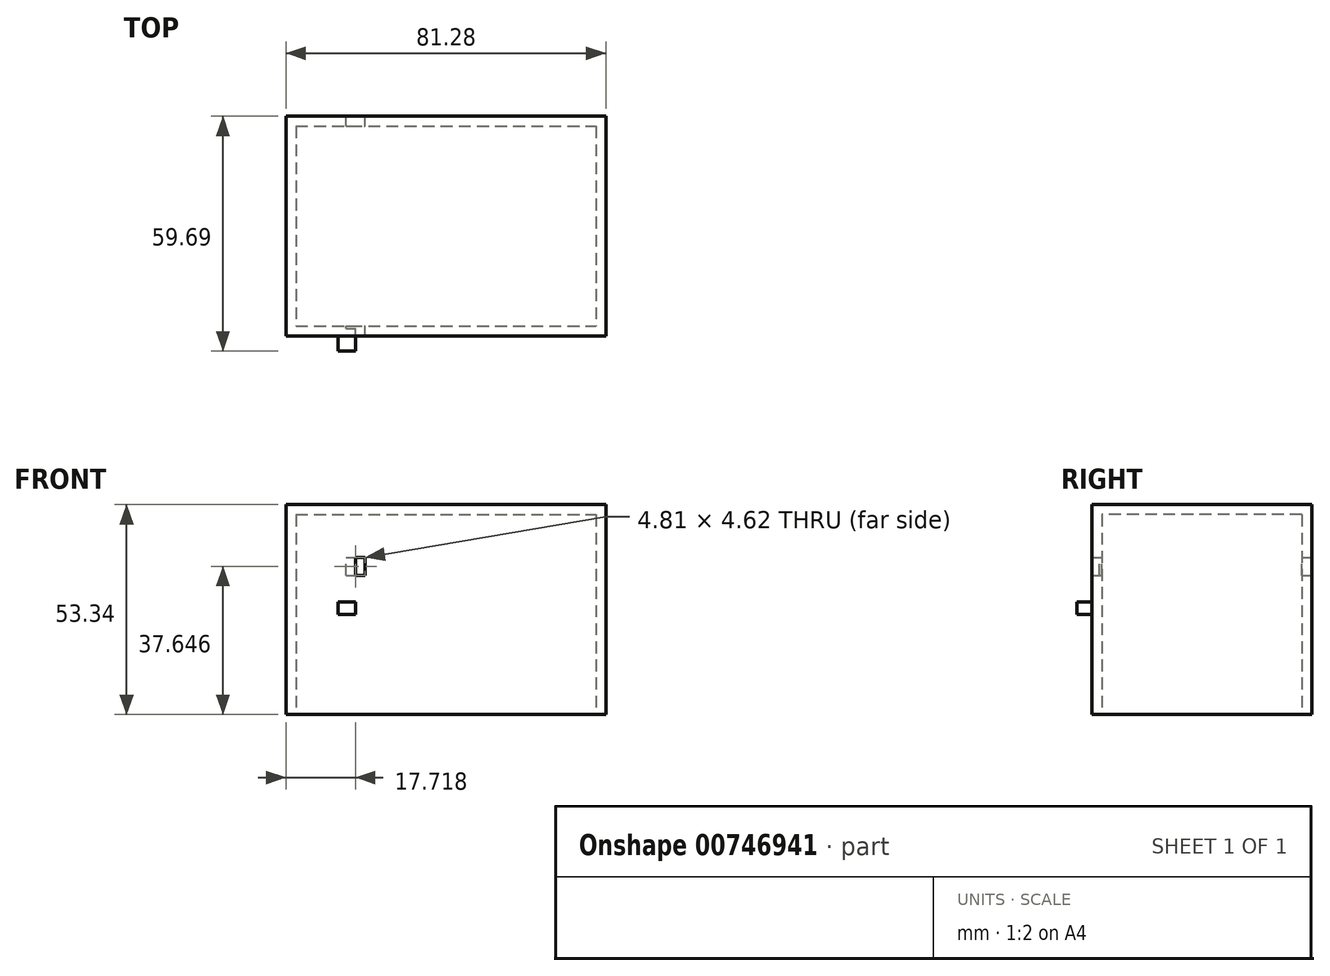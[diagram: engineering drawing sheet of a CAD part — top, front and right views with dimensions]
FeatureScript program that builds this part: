
annotation { "Feature Type Name" : "Feature", "Feature Type Description" : "" }
export const myFeature = defineFeature(function(context is Context, id is Id, definition is map)
    precondition{}
    {
        {
            var Q0;
            Q0=qCreatedBy(makeId("Top.planeOp"),FACE);
            var sketch = newSketch(context, id + "F0", { "sketchPlane" : qUnion([Q0])});
            skLineSegment(sketch, "E0.bottom", {"start": v(-42.28, 23.62) * mm, "end": v(33.92, 23.62) * mm});
            skLineSegment(sketch, "E0.top", {"start": v(-42.28, -27.18) * mm, "end": v(33.92, -27.18) * mm});
            skLineSegment(sketch, "E0.left", {"start": v(-42.28, 23.62) * mm, "end": v(-42.28, -27.18) * mm});
            skLineSegment(sketch, "E0.right", {"start": v(33.92, 23.62) * mm, "end": v(33.92, -27.18) * mm});
            skLineSegment(sketch, "E1.0", {"start": v(-44.82, 26.16) * mm, "end": v(-44.82, -29.72) * mm});
            skLineSegment(sketch, "E1.1", {"start": v(-44.82, 26.16) * mm, "end": v(36.46, 26.16) * mm});
            skLineSegment(sketch, "E1.2", {"start": v(36.46, 26.16) * mm, "end": v(36.46, -29.72) * mm});
            skLineSegment(sketch, "E1.3", {"start": v(-44.82, -29.72) * mm, "end": v(36.46, -29.72) * mm});
            skSolve(sketch);
        }
        {
            var Q0;
            Q0=makeQuery(id+"F0.imprint","IMPRINT",FACE,{"disambiguationData":[TD([[makeQuery(id+"F0.imprint","IMPRINT",EDGE,{"derivedFrom":sQuery(id+"F0.wireOp",EDGE,"E0.bottom")}),1.0]])]});
            extrude(context, id + "F1", {"entities" : qUnion([Q0]), "depth" : 50.8 * mm, "offsetDistance" : 25.4 * mm});
        }
        {
            var Q0;
            Q0 = qSketchRegion(id + "F0", true);
            extrude(context, id + "F2", {"entities" : qUnion([Q0]), "operationType" : NewBodyOperationType.ADD, "depth" : 25.4 * mm, "offsetDistance" : 25.4 * mm});
        }
        {
            var Q0;
            Q0=makeQuery(id+"F1.opExtrude","SWEPT_FACE",FACE,{"disambiguationData":[OSD([sQuery(id+"F0.wireOp",EDGE,"E1.1")])]});
            var sketch = newSketch(context, id + "F3", { "sketchPlane" : qUnion([Q0])});
            skLineSegment(sketch, "E2.bottom", {"start": v(29.5, 35.33) * mm, "end": v(24.7, 35.33) * mm});
            skLineSegment(sketch, "E2.top", {"start": v(29.5, 39.96) * mm, "end": v(24.7, 39.96) * mm});
            skLineSegment(sketch, "E2.left", {"start": v(29.5, 35.33) * mm, "end": v(29.5, 39.96) * mm});
            skLineSegment(sketch, "E2.right", {"start": v(24.7, 35.33) * mm, "end": v(24.7, 39.96) * mm});
            skSolve(sketch);
        }
        {
            var Q0;
            Q0=makeQuery(id+"F3.imprint","IMPRINT",FACE,{"disambiguationData":[TD([[makeQuery(id+"F3.imprint","IMPRINT",EDGE,{"derivedFrom":sQuery(id+"F3.wireOp",EDGE,"E2.bottom")}),-1.0]])]});
            extrude(context, id + "F4", {"entities" : qUnion([Q0]), "operationType" : NewBodyOperationType.REMOVE, "endBound" : BoundingType.THROUGH_ALL, "oppositeDirection" : true, "depth" : 25.4 * mm, "offsetDistance" : 25.4 * mm});
        }
        {
            var Q0;
            Q0=makeQuery(id+"F1.opExtrude","CAP_FACE",FACE,{"disambiguationData":[OSD([sQuery(id+"F0.wireOp",EDGE,"E0.bottom"),sQuery(id+"F0.wireOp",EDGE,"E0.top"),sQuery(id+"F0.wireOp",EDGE,"E0.left"),sQuery(id+"F0.wireOp",EDGE,"E0.right"),sQuery(id+"F0.wireOp",EDGE,"E1.0"),sQuery(id+"F0.wireOp",EDGE,"E1.1"),sQuery(id+"F0.wireOp",EDGE,"E1.2"),sQuery(id+"F0.wireOp",EDGE,"E1.3")])],"isStart":false});
            var sketch = newSketch(context, id + "F5", { "sketchPlane" : qUnion([Q0])});
            skLineSegment(sketch, "E3.bottom", {"start": v(-44.82, 26.16) * mm, "end": v(36.46, 26.16) * mm});
            skLineSegment(sketch, "E3.top", {"start": v(-44.82, -29.72) * mm, "end": v(36.46, -29.72) * mm});
            skLineSegment(sketch, "E3.left", {"start": v(-44.82, 26.16) * mm, "end": v(-44.82, -29.72) * mm});
            skLineSegment(sketch, "E3.right", {"start": v(36.46, 26.16) * mm, "end": v(36.46, -29.72) * mm});
            skSolve(sketch);
        }
        {
            var Q0;
            Q0 = qSketchRegion(id + "F5", true);
            extrude(context, id + "F6", {"entities" : qUnion([Q0]), "depth" : 2.54 * mm, "offsetDistance" : 25.4 * mm});
        }
        {
            var Q0;
            Q0=makeQuery(id+"F6.opExtrude","CAP_FACE",FACE,{"disambiguationData":[OSD([sQuery(id+"F5.wireOp",EDGE,"E3.bottom"),sQuery(id+"F5.wireOp",EDGE,"E3.top"),sQuery(id+"F5.wireOp",EDGE,"E3.left"),sQuery(id+"F5.wireOp",EDGE,"E3.right")])],"isStart":true});
            var sketch = newSketch(context, id + "F7", { "sketchPlane" : qUnion([Q0])});
            skLineSegment(sketch, "E4.bottom", {"start": v(-31.54, 29.72) * mm, "end": v(-27.1, 29.72) * mm});
            skLineSegment(sketch, "E4.top", {"start": v(-31.54, 27.75) * mm, "end": v(-27.1, 27.75) * mm});
            skLineSegment(sketch, "E4.left", {"start": v(-31.54, 29.72) * mm, "end": v(-31.54, 27.75) * mm});
            skLineSegment(sketch, "E4.right", {"start": v(-27.1, 29.72) * mm, "end": v(-27.1, 27.75) * mm});
            skSolve(sketch);
        }
        {
            var Q0;
            Q0 = qSketchRegion(id + "F7", true);
            extrude(context, id + "F8", {"entities" : qUnion([Q0]), "operationType" : NewBodyOperationType.ADD, "depth" : 25.4 * mm, "offsetDistance" : 25.4 * mm});
        }
        {
            var Q0;
            Q0=makeQuery(id+"F8.boolean.opBoolean","MERGE",FACE,{"derivedFrom":[makeQuery(id+"F6.opExtrude","SWEPT_FACE",FACE,{"disambiguationData":[OSD([sQuery(id+"F5.wireOp",EDGE,"E3.top")])]}),makeQuery(id+"F8.opExtrude","SWEPT_FACE",FACE,{"disambiguationData":[OSD([sQuery(id+"F7.wireOp",EDGE,"E4.bottom")])]})]});
            var sketch = newSketch(context, id + "F9", { "sketchPlane" : qUnion([Q0])});
            skLineSegment(sketch, "E5.bottom", {"start": v(-31.54, 28.63) * mm, "end": v(-27.1, 28.63) * mm});
            skLineSegment(sketch, "E5.top", {"start": v(-31.54, 25.4) * mm, "end": v(-27.1, 25.4) * mm});
            skLineSegment(sketch, "E5.left", {"start": v(-31.54, 28.63) * mm, "end": v(-31.54, 25.4) * mm});
            skLineSegment(sketch, "E5.right", {"start": v(-27.1, 28.63) * mm, "end": v(-27.1, 25.4) * mm});
            skSolve(sketch);
        }
        {
            var Q0;
            Q0=makeQuery(id+"F9.imprint","IMPRINT",FACE,{"disambiguationData":[TD([[makeQuery(id+"F9.imprint","IMPRINT",EDGE,{"derivedFrom":sQuery(id+"F9.wireOp",EDGE,"E5.bottom")}),-1.0]])]});
            extrude(context, id + "F10", {"entities" : qUnion([Q0]), "operationType" : NewBodyOperationType.ADD, "depth" : 3.8 * mm, "offsetDistance" : 25.4 * mm});
        }
    });
